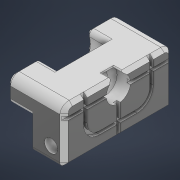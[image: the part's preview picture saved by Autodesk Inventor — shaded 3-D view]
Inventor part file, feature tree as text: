
AUTODESK INVENTOR PART (.ipt)
format: ipt  version: 2022.1 (Build 261234020, 234B)  size: 812,544 bytes
history: native  units: mm
features: delete_face x12, sketch x12, extrude x11, direct_edit x7, move_body x7, other x6, chamfer x6, projected_geometry x6, fillet x4, reference x3, hole x1
ambient origin geometry x8: Origin, YZ Plane, XZ Plane, XY Plane, X Axis, Y Axis, Z Axis, Center Point
bodies: Volumenkörper1 (feature_tree)
feature tree (75):
  other  "Bauteil225.ipt"
  extrude  "Extrusion1"  Depth=10.0mm
  delete_face  "Fläche löschen1"
  delete_face  "Fläche löschen2"
  delete_face  "Fläche löschen3"
  extrude  "Extrusion2"  TaperAngle=0.0deg  [1 undecoded]
  delete_face  "Fläche löschen4"
  delete_face  "Fläche löschen5"
  delete_face  "Fläche löschen6"
  delete_face  "Fläche löschen7"
  extrude  "Extrusion3"  Depth=1.0mm TaperAngle=0.0deg
  extrude  "Extrusion4"  Depth=5.0mm TaperAngle=0.0deg
  direct_edit  "Direktbearbeitung1"
  extrude  "Extrusion5"  Depth=5.0mm TaperAngle=0.0deg
  delete_face  "Fläche löschen8"
  delete_face  "Fläche löschen9"
  extrude  "Extrusion6"  Depth=10.0mm
  hole  "Bohrung1"  [1 undecoded]
  chamfer  "Fase1"  Distance=0.2mm Angle=45.0deg
  chamfer  "Fase2"  Distance=0.6mm Angle=45.0deg
  fillet  "Rundung1"  Radius=2.0mm
  chamfer  "Fase3"  Distance=1.0mm Angle=45.0deg
  fillet  "Rundung2"  Radius=1.0mm
  chamfer  "Fase4"  Distance=0.4mm Angle=45.0deg
  chamfer  "Fase5"  Distance=0.8mm Angle=45.0deg
  extrude  "Extrusion7"  Depth=0.8mm
  extrude  "Extrusion8"  Depth=0.4mm
  extrude  "Extrusion9"  Depth=0.2mm
  fillet  "Rundung3"  Radius=3.0mm
  delete_face  "Fläche löschen10"
  extrude  "Extrusion10"  Depth=0.2mm
  extrude  "Extrusion11"  Depth=0.2mm TaperAngle=0.0deg
  direct_edit  "Direktbearbeitung2"
  chamfer  "Fase6"  Distance=0.05mm
  delete_face  "Fläche löschen11"
  direct_edit  "Direktbearbeitung3"
  direct_edit  "Direktbearbeitung4"
  direct_edit  "Direktbearbeitung5"
  direct_edit  "Direktbearbeitung6"
  delete_face  "Fläche löschen12"
  direct_edit  "Direktbearbeitung7"
  fillet  "Rundung4"  Radius=3.2mm
  other  "Volumenkörper2::Bauteil225.ipt"
  other  "Bezeichnung1"
  sketch  "Skizze1"  dims[d0=10.0mm d1=3.1mm]
  sketch  "Skizze2"  dims[d2=10.0mm d3=0.0mm d4=0.0mm d5=0.0mm]
  projected_geometry  "Projizierte Kontur1"
  sketch  "Skizze3"  dims[d6=6.0mm d7=1.0mm d8=0.0mm]
  sketch  "Skizze4"  dims[d9=12.0mm d10=5.0mm d11=0.0mm]
  projected_geometry  "Projizierte Kontur2"
  sketch  "Skizze5"  dims[d12=0.0mm d13=0.0mm d14=-0.2mm d15=5.0mm d16=0.0mm]
  projected_geometry  "Projizierte Kontur3"
  sketch  "Skizze6"  dims[d17=10.0mm d18=0.0mm d19=3.0mm]
  projected_geometry  "Projizierte Kontur4"
  sketch  "Skizze7"  dims[d20=90.0deg d21=12.8mm]
  projected_geometry  "Projizierte Kontur5"
  sketch  "Skizze8"  dims[d22=12.8mm]
  reference  "Referenz1"
  reference  "Referenz2"
  reference  "Referenz3"
  sketch  "Skizze9"  dims[d23=3.1mm d24=6.0mm d25=5.6mm d26=3.4mm d27=90.0deg d28=3.6mm d29=0.0mm d30=0.25mm d31=0.2mm d32=45.0deg d33=0.6mm d34=1.0mm d35=45.0deg d36=2.0mm d37=1.0mm d38=1.0mm d39=45.0deg d40=1.0mm d41=0.4mm d42=1.0mm d43=45.0deg d44=0.8mm d45=1.0mm d46=45.0deg]
  sketch  "Skizze10"  dims[d47=3.0mm d48=0.8mm]
  sketch  "Skizze11"  dims[d49=0.4mm d50=0.4mm]
  projected_geometry  "Projizierte Kontur6"
  sketch  "Skizze12"  dims[d51=0.8mm d52=0.8mm d53=3.0mm d54=3.8mm d55=0.8mm d56=0.0mm d57=0.05mm d58=3.2mm d59=0.0mm d60=0.3mm d61=5.7mm d62=10.0mm d63=0.0mm d64=0.41mm d65=0.0mm d66=3.14mm d67=0.0mm d68=0.0mm d69=0.0mm d70=0.0mm d71=-0.4mm d72=0.4mm d73=2.0mm d74=45.0deg d75=0.0mm d76=0.0mm d77=-0.6mm d78=0.0mm d79=0.0mm d80=1.0mm d81=0.0mm d82=0.0mm d83=-0.2mm d84=0.0mm d85=0.0mm d86=-0.2mm d87=0.0mm d88=0.0mm d89=0.19mm d90=0.2mm]
  move_body  "Verschieben1"
  other  "<userpath>\Desktop\GitHub\Voron-2-Mods\Panel_Clips\CAD\Inventor\Assembly_Doorhinge.iam"
  other  "Assembly_Doorhinge.iam"
  other  "Doorhinge_Outlet:1"
  move_body  "Verschieben2"
  move_body  "Verschieben3"
  move_body  "Verschieben4"
  move_body  "Verschieben5"
  move_body  "Verschieben6"
  move_body  "Verschieben7"
note: 2 required parameter values undecoded (feature->parameter linkage not recoverable at this tier; creation-order binding heuristic only, values carry confidence <= 0.55)
